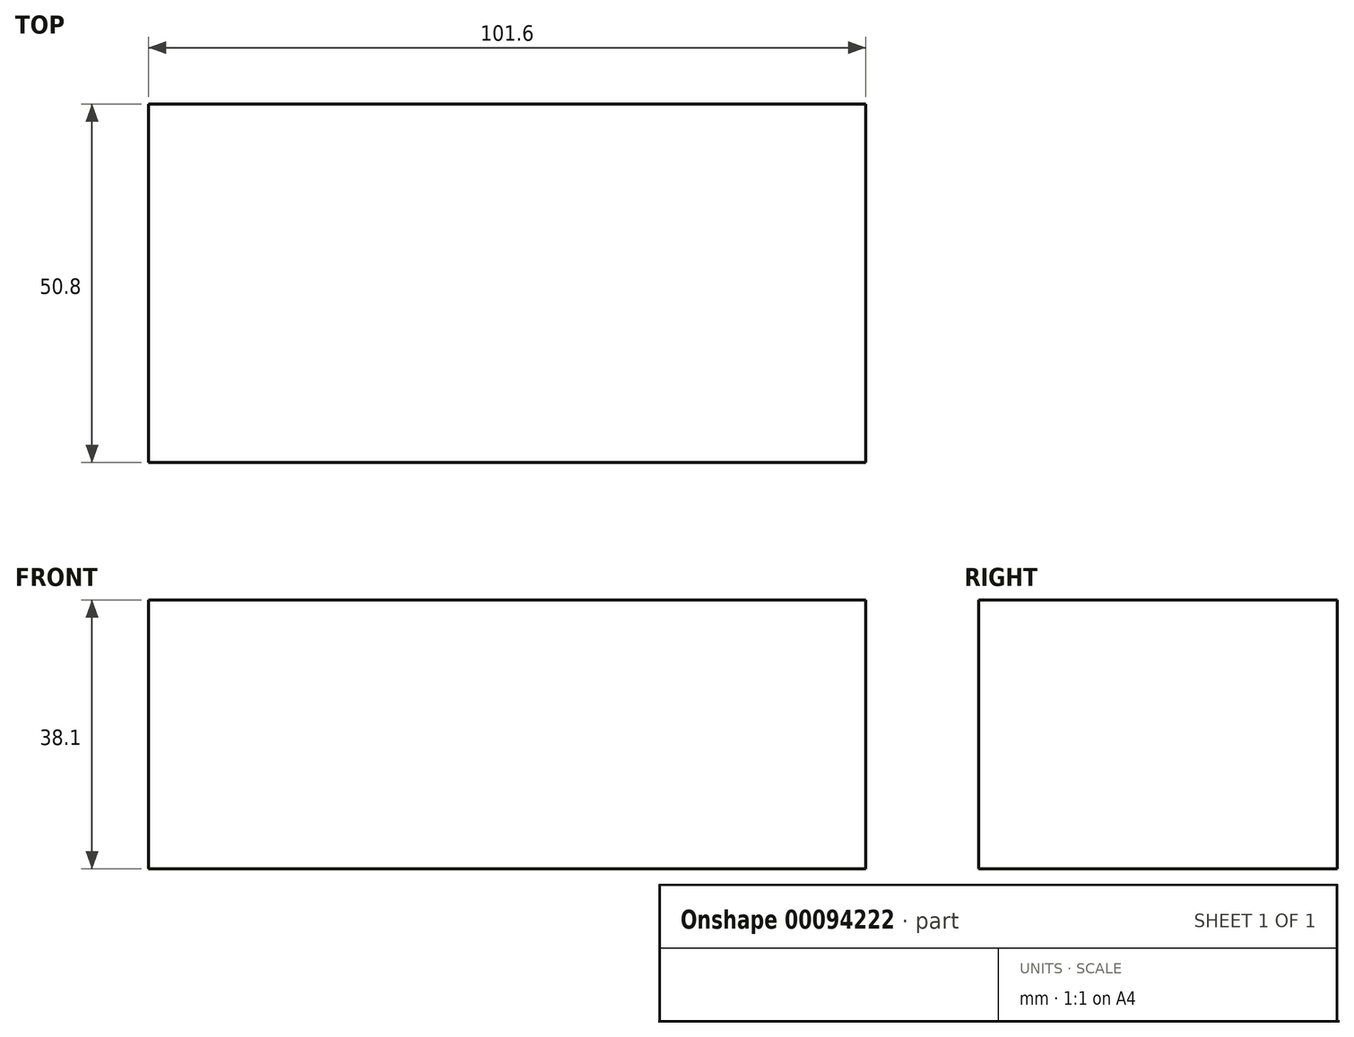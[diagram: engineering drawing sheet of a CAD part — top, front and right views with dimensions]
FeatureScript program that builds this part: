
annotation { "Feature Type Name" : "Feature", "Feature Type Description" : "" }
export const myFeature = defineFeature(function(context is Context, id is Id, definition is map)
    precondition{}
    {
        {
            var Q0;
            Q0=qCreatedBy(makeId("Top.planeOp"),FACE);
            var sketch = newSketch(context, id + "F0", { "sketchPlane" : qUnion([Q0])});
            skLineSegment(sketch, "E0.bottom", {"start": v(-101.6, -50.8) * mm, "end": v(0, -50.8) * mm});
            skLineSegment(sketch, "E0.top", {"start": v(-101.6, 0) * mm, "end": v(0, 0) * mm});
            skLineSegment(sketch, "E0.left", {"start": v(-101.6, -50.8) * mm, "end": v(-101.6, 0) * mm});
            skLineSegment(sketch, "E0.right", {"start": v(0, -50.8) * mm, "end": v(0, 0) * mm});
            skSolve(sketch);
        }
        {
            var Q0;
            Q0=makeQuery(id+"F0.imprint","IMPRINT",FACE,{"disambiguationData":[TD([[makeQuery(id+"F0.imprint","IMPRINT",EDGE,{"derivedFrom":sQuery(id+"F0.wireOp",EDGE,"E0.bottom")}),1.0]])]});
            extrude(context, id + "F1", {"entities" : qUnion([Q0]), "depth" : 38.1 * mm});
        }
    });
